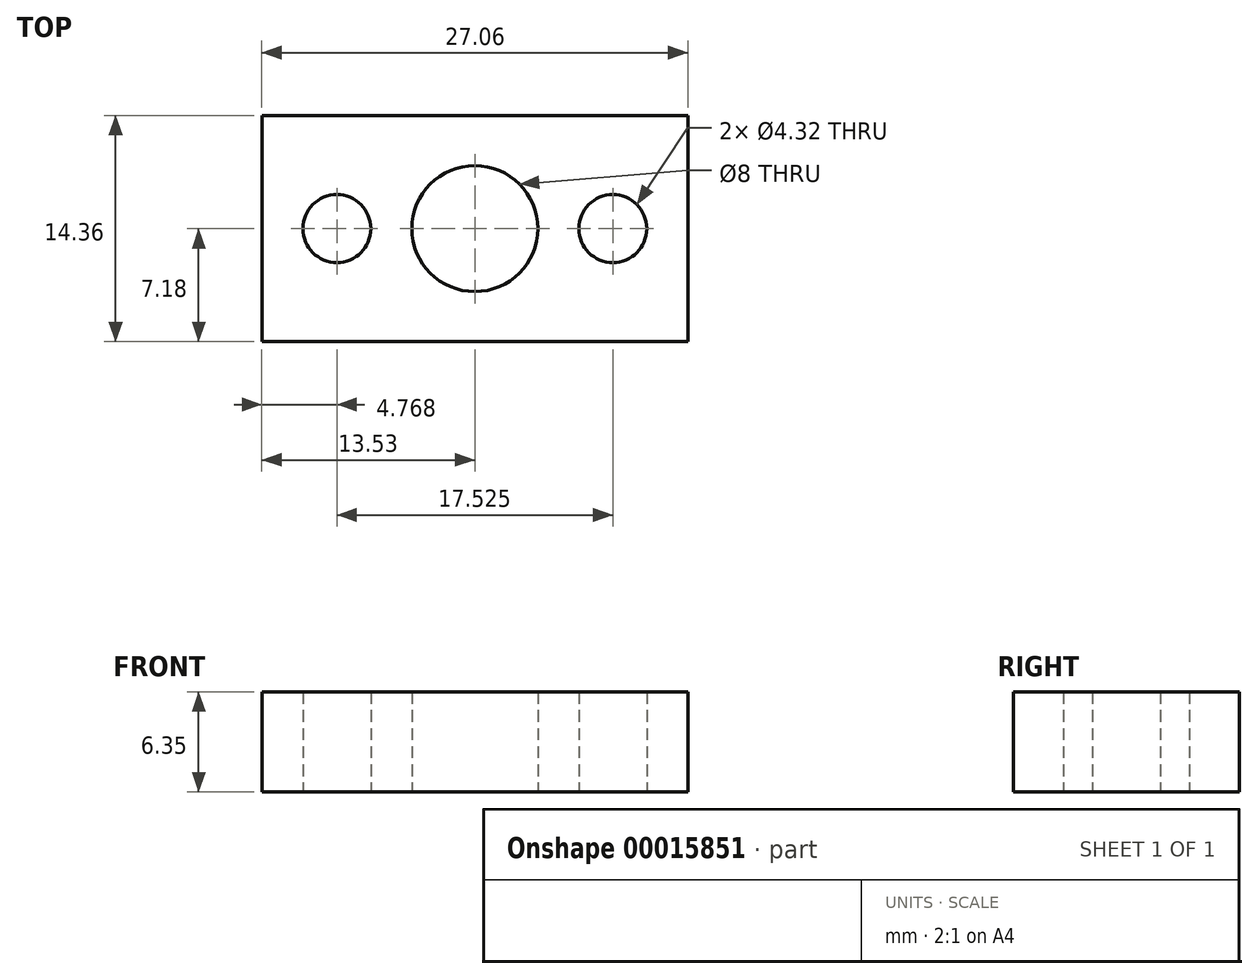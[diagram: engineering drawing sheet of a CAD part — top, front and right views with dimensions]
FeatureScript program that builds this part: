
annotation { "Feature Type Name" : "Feature", "Feature Type Description" : "" }
export const myFeature = defineFeature(function(context is Context, id is Id, definition is map)
    precondition{}
    {
        {
            var Q0;
            Q0=qCreatedBy(makeId("Top.planeOp"),FACE);
            var sketch = newSketch(context, id + "F0", { "sketchPlane" : qUnion([Q0])});
            skLineSegment(sketch, "E0.rect.bottom", {"start": v(13.53, -7.18) * mm, "end": v(-13.53, -7.18) * mm});
            skLineSegment(sketch, "E0.rect.top", {"start": v(13.53, 7.18) * mm, "end": v(-13.53, 7.18) * mm});
            skLineSegment(sketch, "E0.rect.left", {"start": v(13.53, -7.18) * mm, "end": v(13.53, 7.18) * mm});
            skLineSegment(sketch, "E0.rect.right", {"start": v(-13.53, -7.18) * mm, "end": v(-13.53, 7.18) * mm});
            skPoint(sketch, "E0.rect.middle", {"position": v(0, 0) * mm});
            skCircle(sketch, "E1", {"center": v(0, 0) * mm, "radius": 4 * mm});
            skLineSegment(sketch, "E2", {"start": v(-13.53, 0) * mm, "end": v(-8.76, 0) * mm});
            skLineSegment(sketch, "E3", {"start": v(13.53, 0) * mm, "end": v(8.76, 0) * mm});
            skCircle(sketch, "E4", {"center": v(-8.76, 0) * mm, "radius": 2.16 * mm});
            skCircle(sketch, "E5", {"center": v(8.76, 0) * mm, "radius": 2.16 * mm});
            skSolve(sketch);
        }
        {
            var Q0;
            Q0 = qSketchRegion(id + "F0", true);
            extrude(context, id + "F1", {"entities" : qUnion([Q0]), "depth" : 6.35 * mm});
        }
    });
